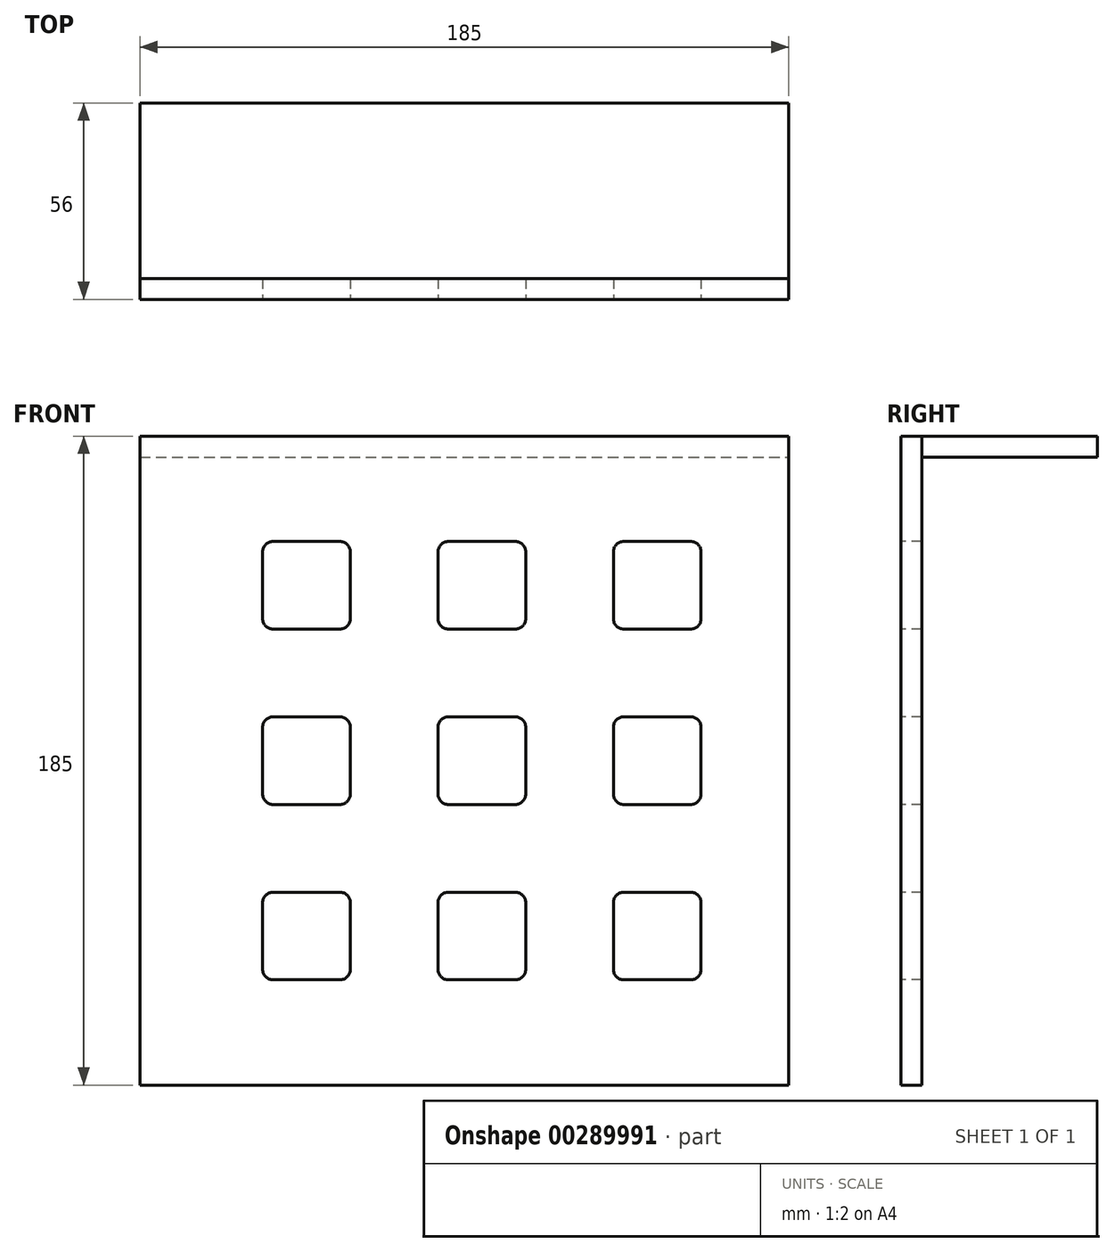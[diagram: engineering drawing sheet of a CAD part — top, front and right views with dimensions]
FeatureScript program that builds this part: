
annotation { "Feature Type Name" : "Feature", "Feature Type Description" : "" }
export const myFeature = defineFeature(function(context is Context, id is Id, definition is map)
    precondition{}
    {
        {
            var Q0;
            Q0=qCreatedBy(makeId("Front.planeOp"),FACE);
            var sketch = newSketch(context, id + "F0", { "sketchPlane" : qUnion([Q0])});
            skLineSegment(sketch, "E0.bottom", {"start": v(0, 0) * mm, "end": v(-185, 0) * mm});
            skLineSegment(sketch, "E0.top", {"start": v(0, -185) * mm, "end": v(-185, -185) * mm});
            skLineSegment(sketch, "E0.left", {"start": v(0, 0) * mm, "end": v(0, -185) * mm});
            skLineSegment(sketch, "E0.right", {"start": v(-185, 0) * mm, "end": v(-185, -185) * mm});
            skSolve(sketch);
        }
        {
            var Q0;
            Q0 = qSketchRegion(id + "F0", true);
            extrude(context, id + "F1", {"entities" : qUnion([Q0]), "depth" : 6 * mm});
        }
        {
            var Q0;
            Q0=makeQuery(id+"F1.opExtrude","CAP_FACE",FACE,{"disambiguationData":[OSD([sQuery(id+"F0.wireOp",EDGE,"E0.bottom"),sQuery(id+"F0.wireOp",EDGE,"E0.top"),sQuery(id+"F0.wireOp",EDGE,"E0.left"),sQuery(id+"F0.wireOp",EDGE,"E0.right")])],"isStart":false});
            var sketch = newSketch(context, id + "F2", { "sketchPlane" : qUnion([Q0])});
            skLineSegment(sketch, "E1", {"start": v(0, 0) * mm, "end": v(-25, 0) * mm});
            skLineSegment(sketch, "E2", {"start": v(-25, -33) * mm, "end": v(-25, -52) * mm});
            skLineSegment(sketch, "E3", {"start": v(-25, -83) * mm, "end": v(-25, -102) * mm});
            skLineSegment(sketch, "E4", {"start": v(-25, -133) * mm, "end": v(-25, -152) * mm});
            skLineSegment(sketch, "E5", {"start": v(-28, -30) * mm, "end": v(-47, -30) * mm});
            skLineSegment(sketch, "E6", {"start": v(-78, -30) * mm, "end": v(-97, -30) * mm});
            skLineSegment(sketch, "E7", {"start": v(-128, -30) * mm, "end": v(-147, -30) * mm});
            skLineSegment(sketch, "E8", {"start": v(-28, -55) * mm, "end": v(-47, -55) * mm});
            skLineSegment(sketch, "E9", {"start": v(-78, -55) * mm, "end": v(-97, -55) * mm});
            skLineSegment(sketch, "E10", {"start": v(-128, -55) * mm, "end": v(-147, -55) * mm});
            skLineSegment(sketch, "E11", {"start": v(-147, -155) * mm, "end": v(-128, -155) * mm});
            skLineSegment(sketch, "E12", {"start": v(-97, -155) * mm, "end": v(-78, -155) * mm});
            skLineSegment(sketch, "E13", {"start": v(-47, -155) * mm, "end": v(-28, -155) * mm});
            skLineSegment(sketch, "E14", {"start": v(-147, -130) * mm, "end": v(-128, -130) * mm});
            skLineSegment(sketch, "E15", {"start": v(-97, -130) * mm, "end": v(-78, -130) * mm});
            skLineSegment(sketch, "E16", {"start": v(-47, -130) * mm, "end": v(-28, -130) * mm});
            skLineSegment(sketch, "E17", {"start": v(-28, -105) * mm, "end": v(-47, -105) * mm});
            skLineSegment(sketch, "E18", {"start": v(-78, -105) * mm, "end": v(-97, -105) * mm});
            skLineSegment(sketch, "E19", {"start": v(-128, -105) * mm, "end": v(-147, -105) * mm});
            skLineSegment(sketch, "E20", {"start": v(-147, -80) * mm, "end": v(-128, -80) * mm});
            skLineSegment(sketch, "E21", {"start": v(-97, -80) * mm, "end": v(-78, -80) * mm});
            skLineSegment(sketch, "E22", {"start": v(-47, -80) * mm, "end": v(-28, -80) * mm});
            skLineSegment(sketch, "E23", {"start": v(-50, -33) * mm, "end": v(-50, -52) * mm});
            skLineSegment(sketch, "E24", {"start": v(-50, -83) * mm, "end": v(-50, -102) * mm});
            skLineSegment(sketch, "E25", {"start": v(-50, -133) * mm, "end": v(-50, -152) * mm});
            skLineSegment(sketch, "E26", {"start": v(-75, -152) * mm, "end": v(-75, -133) * mm});
            skLineSegment(sketch, "E27", {"start": v(-100, -152) * mm, "end": v(-100, -133) * mm});
            skLineSegment(sketch, "E28", {"start": v(-125, -152) * mm, "end": v(-125, -133) * mm});
            skLineSegment(sketch, "E29", {"start": v(-150, -133) * mm, "end": v(-150, -152) * mm});
            skLineSegment(sketch, "E30", {"start": v(-150, -102) * mm, "end": v(-150, -83) * mm});
            skLineSegment(sketch, "E31", {"start": v(-125, -83) * mm, "end": v(-125, -102) * mm});
            skLineSegment(sketch, "E32", {"start": v(-100, -102) * mm, "end": v(-100, -83) * mm});
            skLineSegment(sketch, "E33", {"start": v(-75, -83) * mm, "end": v(-75, -102) * mm});
            skLineSegment(sketch, "E34", {"start": v(-150, -33) * mm, "end": v(-150, -52) * mm});
            skLineSegment(sketch, "E35", {"start": v(-125, -33) * mm, "end": v(-125, -52) * mm});
            skLineSegment(sketch, "E36", {"start": v(-100, -52) * mm, "end": v(-100, -33) * mm});
            skLineSegment(sketch, "E37", {"start": v(-75, -33) * mm, "end": v(-75, -52) * mm});
            skPoint(sketch, "E38.visualSharp", {"position": v(-150, -30) * mm});
            skArc(sketch, "E38.filletArc", {"start": v(-147, -30) * mm, "mid": v(-149.12, -30.88) * mm, "end": v(-150, -33) * mm});
            skPoint(sketch, "E39.visualSharp", {"position": v(-150, -55) * mm});
            skArc(sketch, "E39.filletArc", {"start": v(-150, -52) * mm, "mid": v(-149.12, -54.12) * mm, "end": v(-147, -55) * mm});
            skPoint(sketch, "E40.visualSharp", {"position": v(-125, -55) * mm});
            skArc(sketch, "E40.filletArc", {"start": v(-128, -55) * mm, "mid": v(-125.88, -54.12) * mm, "end": v(-125, -52) * mm});
            skPoint(sketch, "E41.visualSharp", {"position": v(-125, -30) * mm});
            skArc(sketch, "E41.filletArc", {"start": v(-125, -33) * mm, "mid": v(-125.88, -30.88) * mm, "end": v(-128, -30) * mm});
            skPoint(sketch, "E42.visualSharp", {"position": v(-100, -30) * mm});
            skArc(sketch, "E42.filletArc", {"start": v(-97, -30) * mm, "mid": v(-99.12, -30.88) * mm, "end": v(-100, -33) * mm});
            skPoint(sketch, "E43.visualSharp", {"position": v(-75, -30) * mm});
            skArc(sketch, "E43.filletArc", {"start": v(-75, -33) * mm, "mid": v(-75.88, -30.88) * mm, "end": v(-78, -30) * mm});
            skPoint(sketch, "E44.visualSharp", {"position": v(-50, -30) * mm});
            skArc(sketch, "E44.filletArc", {"start": v(-47, -30) * mm, "mid": v(-49.12, -30.88) * mm, "end": v(-50, -33) * mm});
            skPoint(sketch, "E45.visualSharp", {"position": v(-25, -30) * mm});
            skArc(sketch, "E45.filletArc", {"start": v(-25, -33) * mm, "mid": v(-25.88, -30.88) * mm, "end": v(-28, -30) * mm});
            skPoint(sketch, "E46.visualSharp", {"position": v(-25, -55) * mm});
            skArc(sketch, "E46.filletArc", {"start": v(-28, -55) * mm, "mid": v(-25.88, -54.12) * mm, "end": v(-25, -52) * mm});
            skPoint(sketch, "E47.visualSharp", {"position": v(-50, -55) * mm});
            skArc(sketch, "E47.filletArc", {"start": v(-50, -52) * mm, "mid": v(-49.12, -54.12) * mm, "end": v(-47, -55) * mm});
            skPoint(sketch, "E48.visualSharp", {"position": v(-75, -55) * mm});
            skArc(sketch, "E48.filletArc", {"start": v(-78, -55) * mm, "mid": v(-75.88, -54.12) * mm, "end": v(-75, -52) * mm});
            skPoint(sketch, "E49.visualSharp", {"position": v(-100, -55) * mm});
            skArc(sketch, "E49.filletArc", {"start": v(-100, -52) * mm, "mid": v(-99.12, -54.12) * mm, "end": v(-97, -55) * mm});
            skPoint(sketch, "E50.visualSharp", {"position": v(-100, -80) * mm});
            skArc(sketch, "E50.filletArc", {"start": v(-97, -80) * mm, "mid": v(-99.12, -80.88) * mm, "end": v(-100, -83) * mm});
            skPoint(sketch, "E51.visualSharp", {"position": v(-75, -80) * mm});
            skArc(sketch, "E51.filletArc", {"start": v(-75, -83) * mm, "mid": v(-75.88, -80.88) * mm, "end": v(-78, -80) * mm});
            skPoint(sketch, "E52.visualSharp", {"position": v(-75, -105) * mm});
            skArc(sketch, "E52.filletArc", {"start": v(-78, -105) * mm, "mid": v(-75.88, -104.12) * mm, "end": v(-75, -102) * mm});
            skPoint(sketch, "E53.visualSharp", {"position": v(-100, -105) * mm});
            skArc(sketch, "E53.filletArc", {"start": v(-100, -102) * mm, "mid": v(-99.12, -104.12) * mm, "end": v(-97, -105) * mm});
            skPoint(sketch, "E54.visualSharp", {"position": v(-125, -105) * mm});
            skArc(sketch, "E54.filletArc", {"start": v(-128, -105) * mm, "mid": v(-125.88, -104.12) * mm, "end": v(-125, -102) * mm});
            skPoint(sketch, "E55.visualSharp", {"position": v(-125, -80) * mm});
            skArc(sketch, "E55.filletArc", {"start": v(-125, -83) * mm, "mid": v(-125.88, -80.88) * mm, "end": v(-128, -80) * mm});
            skPoint(sketch, "E56.visualSharp", {"position": v(-150, -80) * mm});
            skArc(sketch, "E56.filletArc", {"start": v(-147, -80) * mm, "mid": v(-149.12, -80.88) * mm, "end": v(-150, -83) * mm});
            skPoint(sketch, "E57.visualSharp", {"position": v(-150, -105) * mm});
            skArc(sketch, "E57.filletArc", {"start": v(-150, -102) * mm, "mid": v(-149.12, -104.12) * mm, "end": v(-147, -105) * mm});
            skPoint(sketch, "E58.visualSharp", {"position": v(-150, -130) * mm});
            skArc(sketch, "E58.filletArc", {"start": v(-147, -130) * mm, "mid": v(-149.12, -130.88) * mm, "end": v(-150, -133) * mm});
            skPoint(sketch, "E59.visualSharp", {"position": v(-150, -155) * mm});
            skArc(sketch, "E59.filletArc", {"start": v(-150, -152) * mm, "mid": v(-149.12, -154.12) * mm, "end": v(-147, -155) * mm});
            skPoint(sketch, "E60.visualSharp", {"position": v(-125, -155) * mm});
            skArc(sketch, "E60.filletArc", {"start": v(-128, -155) * mm, "mid": v(-125.88, -154.12) * mm, "end": v(-125, -152) * mm});
            skPoint(sketch, "E61.visualSharp", {"position": v(-125, -130) * mm});
            skArc(sketch, "E61.filletArc", {"start": v(-125, -133) * mm, "mid": v(-125.88, -130.88) * mm, "end": v(-128, -130) * mm});
            skPoint(sketch, "E62.visualSharp", {"position": v(-100, -130) * mm});
            skArc(sketch, "E62.filletArc", {"start": v(-97, -130) * mm, "mid": v(-99.12, -130.88) * mm, "end": v(-100, -133) * mm});
            skPoint(sketch, "E63.visualSharp", {"position": v(-75, -130) * mm});
            skArc(sketch, "E63.filletArc", {"start": v(-75, -133) * mm, "mid": v(-75.88, -130.88) * mm, "end": v(-78, -130) * mm});
            skPoint(sketch, "E64.visualSharp", {"position": v(-75, -155) * mm});
            skArc(sketch, "E64.filletArc", {"start": v(-78, -155) * mm, "mid": v(-75.88, -154.12) * mm, "end": v(-75, -152) * mm});
            skPoint(sketch, "E65.visualSharp", {"position": v(-100, -155) * mm});
            skArc(sketch, "E65.filletArc", {"start": v(-100, -152) * mm, "mid": v(-99.12, -154.12) * mm, "end": v(-97, -155) * mm});
            skPoint(sketch, "E66.visualSharp", {"position": v(-50, -155) * mm});
            skArc(sketch, "E66.filletArc", {"start": v(-50, -152) * mm, "mid": v(-49.12, -154.12) * mm, "end": v(-47, -155) * mm});
            skPoint(sketch, "E67.visualSharp", {"position": v(-25, -155) * mm});
            skArc(sketch, "E67.filletArc", {"start": v(-28, -155) * mm, "mid": v(-25.88, -154.12) * mm, "end": v(-25, -152) * mm});
            skPoint(sketch, "E68.visualSharp", {"position": v(-25, -130) * mm});
            skArc(sketch, "E68.filletArc", {"start": v(-25, -133) * mm, "mid": v(-25.88, -130.88) * mm, "end": v(-28, -130) * mm});
            skPoint(sketch, "E69.visualSharp", {"position": v(-50, -130) * mm});
            skArc(sketch, "E69.filletArc", {"start": v(-47, -130) * mm, "mid": v(-49.12, -130.88) * mm, "end": v(-50, -133) * mm});
            skPoint(sketch, "E70.visualSharp", {"position": v(-50, -105) * mm});
            skArc(sketch, "E70.filletArc", {"start": v(-50, -102) * mm, "mid": v(-49.12, -104.12) * mm, "end": v(-47, -105) * mm});
            skPoint(sketch, "E71.visualSharp", {"position": v(-50, -80) * mm});
            skArc(sketch, "E71.filletArc", {"start": v(-47, -80) * mm, "mid": v(-49.12, -80.88) * mm, "end": v(-50, -83) * mm});
            skPoint(sketch, "E72.visualSharp", {"position": v(-25, -80) * mm});
            skArc(sketch, "E72.filletArc", {"start": v(-25, -83) * mm, "mid": v(-25.88, -80.88) * mm, "end": v(-28, -80) * mm});
            skPoint(sketch, "E73.visualSharp", {"position": v(-25, -105) * mm});
            skArc(sketch, "E73.filletArc", {"start": v(-28, -105) * mm, "mid": v(-25.88, -104.12) * mm, "end": v(-25, -102) * mm});
            skSolve(sketch);
        }
        {
            var Q0;
            Q0=makeQuery(id+"F2.imprint","IMPRINT",FACE,{"disambiguationData":[TD([[makeQuery(id+"F2.imprint","IMPRINT",EDGE,{"derivedFrom":sQuery(id+"F2.wireOp",EDGE,"E7")}),1.0]])]});
            var Q1;
            Q1=makeQuery(id+"F2.imprint","IMPRINT",FACE,{"disambiguationData":[TD([[makeQuery(id+"F2.imprint","IMPRINT",EDGE,{"derivedFrom":sQuery(id+"F2.wireOp",EDGE,"E6")}),1.0]])]});
            var Q2;
            Q2=makeQuery(id+"F2.imprint","IMPRINT",FACE,{"disambiguationData":[TD([[makeQuery(id+"F2.imprint","IMPRINT",EDGE,{"derivedFrom":sQuery(id+"F2.wireOp",EDGE,"E2")}),-1.0]])]});
            var Q3;
            Q3=makeQuery(id+"F2.imprint","IMPRINT",FACE,{"disambiguationData":[TD([[makeQuery(id+"F2.imprint","IMPRINT",EDGE,{"derivedFrom":sQuery(id+"F2.wireOp",EDGE,"E3")}),-1.0]])]});
            var Q4;
            Q4=makeQuery(id+"F2.imprint","IMPRINT",FACE,{"disambiguationData":[TD([[makeQuery(id+"F2.imprint","IMPRINT",EDGE,{"derivedFrom":sQuery(id+"F2.wireOp",EDGE,"E18")}),-1.0]])]});
            var Q5;
            Q5=makeQuery(id+"F2.imprint","IMPRINT",FACE,{"disambiguationData":[TD([[makeQuery(id+"F2.imprint","IMPRINT",EDGE,{"derivedFrom":sQuery(id+"F2.wireOp",EDGE,"E19")}),-1.0]])]});
            var Q6;
            Q6=makeQuery(id+"F2.imprint","IMPRINT",FACE,{"disambiguationData":[TD([[makeQuery(id+"F2.imprint","IMPRINT",EDGE,{"derivedFrom":sQuery(id+"F2.wireOp",EDGE,"E11")}),1.0]])]});
            var Q7;
            Q7=makeQuery(id+"F2.imprint","IMPRINT",FACE,{"disambiguationData":[TD([[makeQuery(id+"F2.imprint","IMPRINT",EDGE,{"derivedFrom":sQuery(id+"F2.wireOp",EDGE,"E12")}),1.0]])]});
            var Q8;
            Q8=makeQuery(id+"F2.imprint","IMPRINT",FACE,{"disambiguationData":[TD([[makeQuery(id+"F2.imprint","IMPRINT",EDGE,{"derivedFrom":sQuery(id+"F2.wireOp",EDGE,"E4")}),-1.0]])]});
            extrude(context, id + "F3", {"entities" : qUnion([Q0, Q1, Q2, Q3, Q4, Q5, Q6, Q7, Q8]), "operationType" : NewBodyOperationType.REMOVE, "oppositeDirection" : true, "depth" : 25 * mm});
        }
        {
            var Q0;
            Q0=qCreatedBy(makeId("Right.planeOp"),FACE);
            var sketch = newSketch(context, id + "F4", { "sketchPlane" : qUnion([Q0])});
            skLineSegment(sketch, "E74.bottom", {"start": v(0, 0) * mm, "end": v(50, 0) * mm});
            skLineSegment(sketch, "E74.top", {"start": v(0, -6) * mm, "end": v(50, -6) * mm});
            skLineSegment(sketch, "E74.left", {"start": v(0, 0) * mm, "end": v(0, -6) * mm});
            skLineSegment(sketch, "E74.right", {"start": v(50, 0) * mm, "end": v(50, -6) * mm});
            skSolve(sketch);
        }
        {
            var Q0;
            Q0 = qSketchRegion(id + "F4", true);
            extrude(context, id + "F5", {"entities" : qUnion([Q0]), "oppositeDirection" : true, "depth" : 185 * mm});
        }
    });
